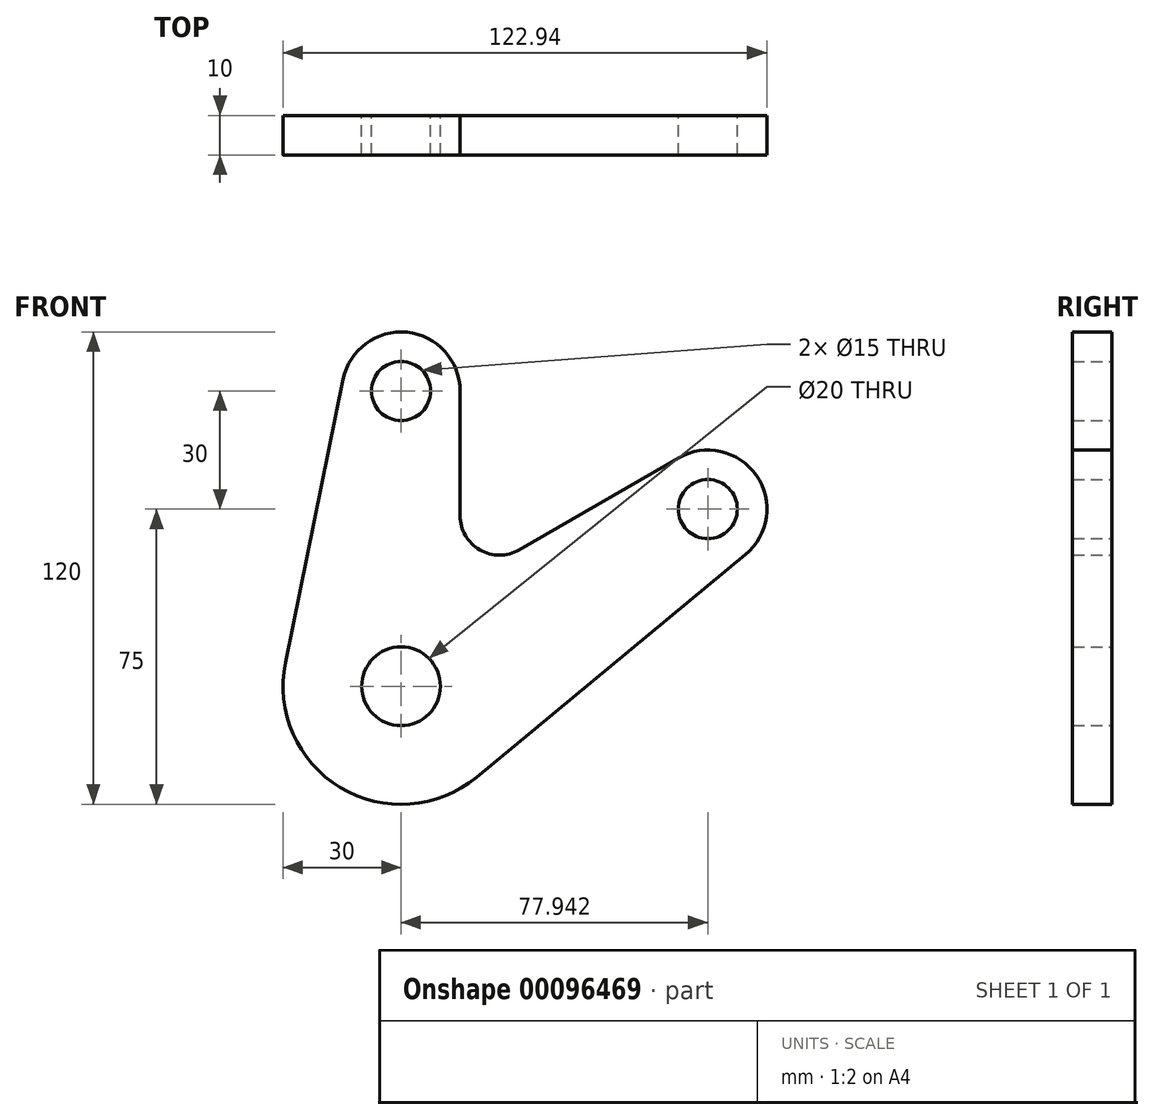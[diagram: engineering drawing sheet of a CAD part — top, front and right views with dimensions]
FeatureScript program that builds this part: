
annotation { "Feature Type Name" : "Feature", "Feature Type Description" : "" }
export const myFeature = defineFeature(function(context is Context, id is Id, definition is map)
    precondition{}
    {
        {
            var Q0;
            Q0=qCreatedBy(makeId("Front.planeOp"),FACE);
            var sketch = newSketch(context, id + "F0", { "sketchPlane" : qUnion([Q0])});
            skCircle(sketch, "E0", {"center": v(0, 0) * mm, "radius": 10 * mm});
            skLineSegment(sketch, "E1", {"start": v(19.12, -23.12) * mm, "end": v(87.5, 33.44) * mm});
            skLineSegment(sketch, "E2", {"start": v(-29.4, 6) * mm, "end": v(-14.7, 78) * mm});
            skArc(sketch, "E3", {"start": v(-29.4, 6) * mm, "mid": v(-15.44, -25.72) * mm, "end": v(19.12, -23.12) * mm});
            skLineSegment(sketch, "E4", {"start": v(15, 43.3) * mm, "end": v(15, 75) * mm});
            skArc(sketch, "E5", {"start": v(15, 75) * mm, "mid": v(1.5, 89.92) * mm, "end": v(-14.7, 78) * mm});
            skArc(sketch, "E6", {"start": v(87.5, 33.44) * mm, "mid": v(90.26, 53.56) * mm, "end": v(70.44, 58) * mm});
            skCircle(sketch, "E7", {"center": v(0, 75) * mm, "radius": 7.5 * mm});
            skCircle(sketch, "E8", {"center": v(77.94, 45) * mm, "radius": 7.5 * mm});
            skLineSegment(sketch, "E9", {"start": v(0, 75) * mm, "end": v(0, 0) * mm, "construction": true});
            skLineSegment(sketch, "E10", {"start": v(77.94, 45) * mm, "end": v(0, 0) * mm, "construction": true});
            skArc(sketch, "E11", {"start": v(15, 43.3) * mm, "mid": v(20, 34.64) * mm, "end": v(30, 34.64) * mm});
            skLineSegment(sketch, "E12", {"start": v(30, 34.64) * mm, "end": v(70.44, 58) * mm});
            skSolve(sketch);
        }
        {
            var Q0;
            Q0 = qSketchRegion(id + "F0", true);
            extrude(context, id + "F1", {"entities" : qUnion([Q0]), "depth" : 10 * mm});
        }
    });
